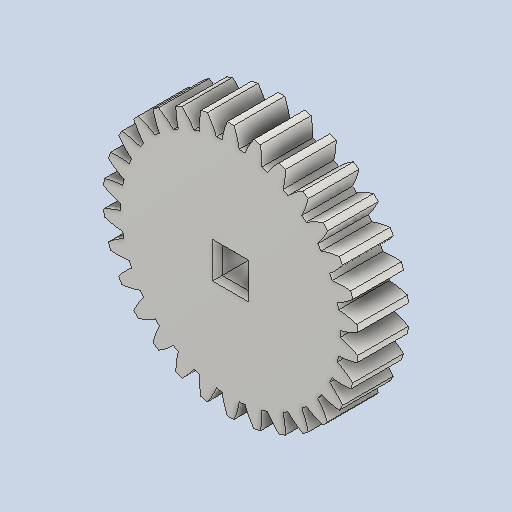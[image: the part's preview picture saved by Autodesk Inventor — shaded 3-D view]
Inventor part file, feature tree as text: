
AUTODESK INVENTOR PART (.ipt)
format: ipt  version: 2022 (Build 260153000, 153)  size: 333,312 bytes
history: native  units: in
note: dims shown in document units (in); Inventor stores cm internally (conversion verified against a paired STEP export)
features: other x12, sketch x3, plane x3
ambient origin geometry x8: Origin, YZ Plane, XZ Plane, XY Plane, X Axis, Y Axis, Z Axis, Center Point
bodies: Solid1 (feature_tree)
feature tree (18):
  other  "Spur Gear1"
  other  "Solid1::Spur Gear1"
  other  "TaggingFeature1"
  sketch  "Sketch1"  dims[d0=0.3937in]
  sketch  "Sketch2"  dims[d9=0.0in d14=0.0in d15=1.0in d16=0.0in d17=0.0in d18=0.0in d19=1.0in]
  sketch  "Sketch3"
  plane  "XZ Plane_1"
  plane  "Work Plane2"
  plane  "Work Plane3"
  other  "Srf1"
  other  "Srf1::Derived"
  other  "Start plane iMate"
  other  "Distance iMate"
  other  "Position iMate"
  other  "Mesh iMate"
  other  "Axis iMate"
  other  "Mesh iMate2"
  other  "Align iMate"
